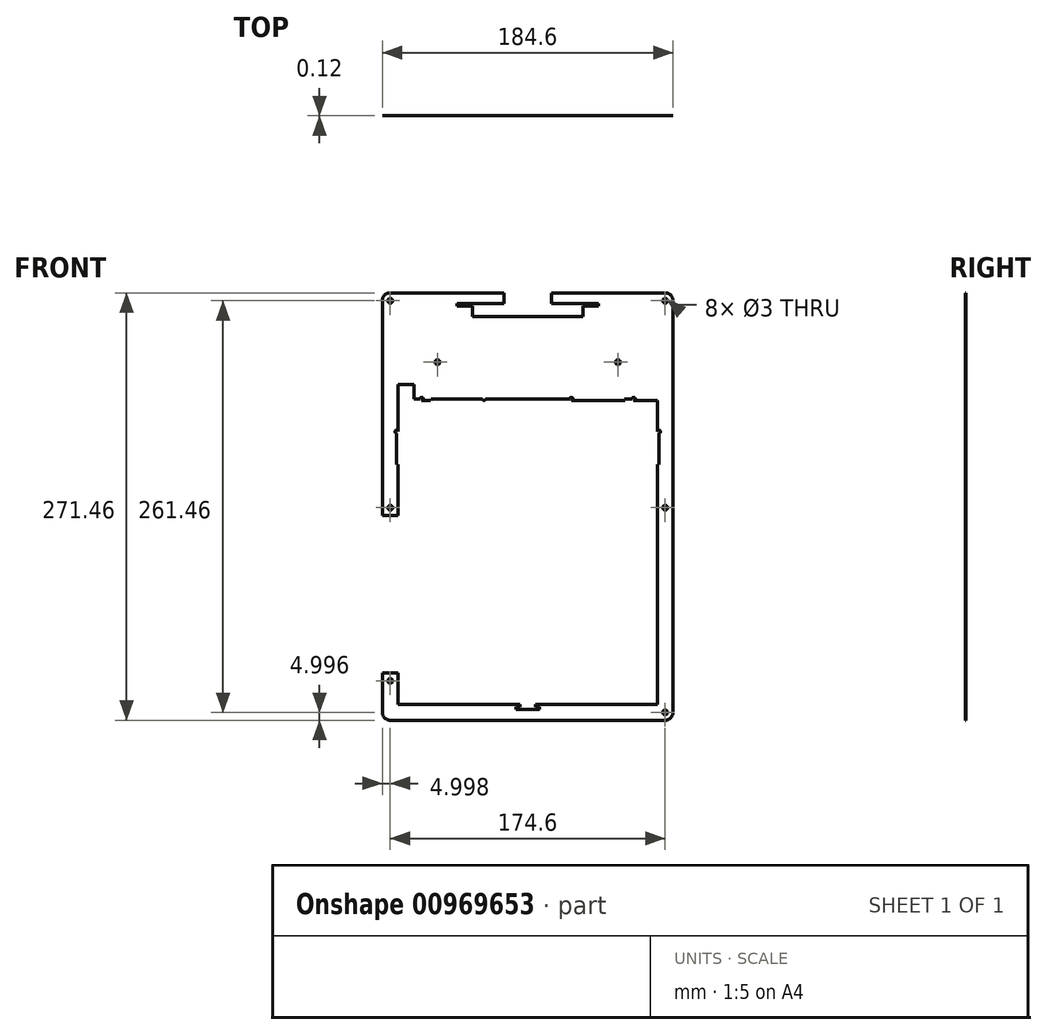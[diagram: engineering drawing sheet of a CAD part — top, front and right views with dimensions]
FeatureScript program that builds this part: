
annotation { "Feature Type Name" : "Feature", "Feature Type Description" : "" }
export const myFeature = defineFeature(function(context is Context, id is Id, definition is map)
    precondition{}
    {
        {
            var Q0;
            Q0=qCreatedBy(makeId("Front.planeOp"),FACE);
            var sketch = newSketch(context, id + "F0", { "sketchPlane" : qUnion([Q0])});
            skLineSegment(sketch, "E0.bottom", {"start": v(-64.57, 145.19) * mm, "end": v(110.03, 145.19) * mm});
            skLineSegment(sketch, "E0.top", {"start": v(-64.57, -126.27) * mm, "end": v(110.03, -126.27) * mm});
            skLineSegment(sketch, "E0.left", {"start": v(-69.57, 140.19) * mm, "end": v(-69.57, -121.27) * mm});
            skLineSegment(sketch, "E0.right", {"start": v(115.03, 140.19) * mm, "end": v(115.03, -121.27) * mm});
            skPoint(sketch, "E1.visualSharp", {"position": v(-69.57, 145.19) * mm});
            skArc(sketch, "E1.filletArc", {"start": v(-64.57, 145.19) * mm, "mid": v(-68.1, 143.72) * mm, "end": v(-69.57, 140.19) * mm});
            skPoint(sketch, "E2.visualSharp", {"position": v(115.03, 145.19) * mm});
            skArc(sketch, "E2.filletArc", {"start": v(115.03, 140.19) * mm, "mid": v(113.56, 143.72) * mm, "end": v(110.03, 145.19) * mm});
            skPoint(sketch, "E3.visualSharp", {"position": v(-69.57, -126.27) * mm});
            skArc(sketch, "E3.filletArc", {"start": v(-69.57, -121.27) * mm, "mid": v(-68.1, -124.8) * mm, "end": v(-64.57, -126.27) * mm});
            skPoint(sketch, "E4.visualSharp", {"position": v(115.03, -126.27) * mm});
            skArc(sketch, "E4.filletArc", {"start": v(110.03, -126.27) * mm, "mid": v(113.56, -124.8) * mm, "end": v(115.03, -121.27) * mm});
            skCircle(sketch, "E5", {"center": v(-64.57, 140.19) * mm, "radius": 1.5 * mm});
            skCircle(sketch, "E6", {"center": v(110.03, 140.19) * mm, "radius": 1.5 * mm});
            skCircle(sketch, "E7", {"center": v(110.03, -121.27) * mm, "radius": 1.5 * mm});
            skCircle(sketch, "E8", {"center": v(-64.57, -101.27) * mm, "radius": 1.5 * mm});
            skLineSegment(sketch, "E9.bottom", {"start": v(-59.57, 135.19) * mm, "end": v(105.03, 135.19) * mm});
            skLineSegment(sketch, "E9.top", {"start": v(-59.57, -116.27) * mm, "end": v(105.03, -116.27) * mm});
            skLineSegment(sketch, "E9.left", {"start": v(-59.57, 135.19) * mm, "end": v(-59.57, -116.27) * mm});
            skLineSegment(sketch, "E9.right", {"start": v(105.03, 135.19) * mm, "end": v(105.03, -116.27) * mm});
            skLineSegment(sketch, "E10.bottom", {"start": v(17.73, -116.27) * mm, "end": v(27.73, -116.27) * mm});
            skLineSegment(sketch, "E10.top", {"start": v(17.73, -117.75) * mm, "end": v(27.73, -117.75) * mm});
            skLineSegment(sketch, "E10.left", {"start": v(17.73, -116.27) * mm, "end": v(17.73, -117.75) * mm});
            skLineSegment(sketch, "E10.right", {"start": v(27.73, -116.27) * mm, "end": v(27.73, -117.75) * mm});
            skLineSegment(sketch, "E11.bottom", {"start": v(15.23, -117.75) * mm, "end": v(30.23, -117.75) * mm});
            skLineSegment(sketch, "E11.top", {"start": v(15.23, -119.35) * mm, "end": v(30.23, -119.35) * mm});
            skLineSegment(sketch, "E11.left", {"start": v(15.23, -117.75) * mm, "end": v(15.23, -119.35) * mm});
            skLineSegment(sketch, "E11.right", {"start": v(30.23, -117.75) * mm, "end": v(30.23, -119.35) * mm});
            skLineSegment(sketch, "E12.bottom", {"start": v(-12.27, 135.19) * mm, "end": v(57.73, 135.19) * mm});
            skLineSegment(sketch, "E12.top", {"start": v(-12.27, 136.79) * mm, "end": v(57.73, 136.79) * mm});
            skLineSegment(sketch, "E12.left", {"start": v(-12.27, 135.19) * mm, "end": v(-12.27, 136.79) * mm});
            skLineSegment(sketch, "E12.right", {"start": v(57.73, 135.19) * mm, "end": v(57.73, 136.79) * mm});
            skLineSegment(sketch, "E13.bottom", {"start": v(-22.27, 138.49) * mm, "end": v(67.73, 138.49) * mm});
            skLineSegment(sketch, "E13.top", {"start": v(-22.27, 136.79) * mm, "end": v(67.73, 136.79) * mm});
            skLineSegment(sketch, "E13.left", {"start": v(-22.27, 138.49) * mm, "end": v(-22.27, 136.79) * mm});
            skLineSegment(sketch, "E13.right", {"start": v(67.73, 138.49) * mm, "end": v(67.73, 136.79) * mm});
            skLineSegment(sketch, "E14.bottom", {"start": v(7.73, 145.19) * mm, "end": v(37.73, 145.19) * mm});
            skLineSegment(sketch, "E14.top", {"start": v(7.73, 138.49) * mm, "end": v(37.73, 138.49) * mm});
            skLineSegment(sketch, "E14.left", {"start": v(7.73, 145.19) * mm, "end": v(7.73, 138.49) * mm});
            skLineSegment(sketch, "E14.right", {"start": v(37.73, 145.19) * mm, "end": v(37.73, 138.49) * mm});
            skLineSegment(sketch, "E15.bottom", {"start": v(-59.57, 36.13) * mm, "end": v(105.03, 36.13) * mm});
            skLineSegment(sketch, "E15.top", {"start": v(-59.57, 35.13) * mm, "end": v(105.03, 35.13) * mm});
            skLineSegment(sketch, "E15.left", {"start": v(-59.57, 36.13) * mm, "end": v(-59.57, 35.13) * mm});
            skLineSegment(sketch, "E15.right", {"start": v(105.03, 36.13) * mm, "end": v(105.03, 35.13) * mm});
            skLineSegment(sketch, "E16.bottom", {"start": v(-62.57, 35.13) * mm, "end": v(108.03, 35.13) * mm});
            skLineSegment(sketch, "E16.top", {"start": v(-62.57, 33.13) * mm, "end": v(108.03, 33.13) * mm});
            skLineSegment(sketch, "E16.left", {"start": v(-62.57, 35.13) * mm, "end": v(-62.57, 33.13) * mm});
            skLineSegment(sketch, "E16.right", {"start": v(108.03, 35.13) * mm, "end": v(108.03, 33.13) * mm});
            skLineSegment(sketch, "E17.bottom", {"start": v(108.03, 33.13) * mm, "end": v(105.03, 33.13) * mm});
            skLineSegment(sketch, "E17.top", {"start": v(108.03, 34.53) * mm, "end": v(105.03, 34.53) * mm});
            skLineSegment(sketch, "E17.left", {"start": v(108.03, 33.13) * mm, "end": v(108.03, 34.53) * mm});
            skLineSegment(sketch, "E17.right", {"start": v(105.03, 33.13) * mm, "end": v(105.03, 34.53) * mm});
            skLineSegment(sketch, "E18.bottom", {"start": v(-62.57, 33.13) * mm, "end": v(-59.57, 33.13) * mm});
            skLineSegment(sketch, "E18.top", {"start": v(-62.57, 34.53) * mm, "end": v(-59.57, 34.53) * mm});
            skLineSegment(sketch, "E18.left", {"start": v(-62.57, 33.13) * mm, "end": v(-62.57, 34.53) * mm});
            skLineSegment(sketch, "E18.right", {"start": v(-59.57, 33.13) * mm, "end": v(-59.57, 34.53) * mm});
            skLineSegment(sketch, "E19.top", {"start": v(-59.57, 66.13) * mm, "end": v(105.03, 66.13) * mm});
            skLineSegment(sketch, "E19.left", {"start": v(-59.57, 36.13) * mm, "end": v(-59.57, 66.13) * mm});
            skLineSegment(sketch, "E19.right", {"start": v(105.03, 36.13) * mm, "end": v(105.03, 66.13) * mm});
            skLineSegment(sketch, "E20.top", {"start": v(-59.57, 76.88) * mm, "end": v(105.03, 76.88) * mm});
            skLineSegment(sketch, "E20.left", {"start": v(-59.57, 36.13) * mm, "end": v(-59.57, 76.88) * mm});
            skLineSegment(sketch, "E20.right", {"start": v(105.03, 36.13) * mm, "end": v(105.03, 76.88) * mm});
            skLineSegment(sketch, "E21.bottom", {"start": v(-52.27, 66.13) * mm, "end": v(97.73, 66.13) * mm});
            skLineSegment(sketch, "E21.top", {"start": v(-52.27, 36.13) * mm, "end": v(97.73, 36.13) * mm});
            skLineSegment(sketch, "E21.left", {"start": v(-52.27, 66.13) * mm, "end": v(-52.27, 36.13) * mm});
            skLineSegment(sketch, "E21.right", {"start": v(97.73, 66.13) * mm, "end": v(97.73, 36.13) * mm});
            skLineSegment(sketch, "E22.bottom", {"start": v(-55.27, 36.13) * mm, "end": v(100.73, 36.13) * mm});
            skLineSegment(sketch, "E22.top", {"start": v(-55.27, 69.13) * mm, "end": v(100.73, 69.13) * mm});
            skLineSegment(sketch, "E22.left", {"start": v(-55.27, 36.13) * mm, "end": v(-55.27, 69.13) * mm});
            skLineSegment(sketch, "E22.right", {"start": v(100.73, 36.13) * mm, "end": v(100.73, 69.13) * mm});
            skLineSegment(sketch, "E23.bottom", {"start": v(-58.27, 72.13) * mm, "end": v(103.73, 72.13) * mm});
            skLineSegment(sketch, "E23.top", {"start": v(-58.27, 33.13) * mm, "end": v(103.73, 33.13) * mm});
            skLineSegment(sketch, "E23.left", {"start": v(-58.27, 72.13) * mm, "end": v(-58.27, 33.13) * mm});
            skLineSegment(sketch, "E23.right", {"start": v(103.73, 72.13) * mm, "end": v(103.73, 33.13) * mm});
            skLineSegment(sketch, "E24.top", {"start": v(-12.27, 130.19) * mm, "end": v(57.73, 130.19) * mm});
            skLineSegment(sketch, "E24.left", {"start": v(-12.27, 135.19) * mm, "end": v(-12.27, 130.19) * mm});
            skLineSegment(sketch, "E24.right", {"start": v(57.73, 135.19) * mm, "end": v(57.73, 130.19) * mm});
            skLineSegment(sketch, "E25.bottom", {"start": v(-59.57, 33.13) * mm, "end": v(105.03, 33.13) * mm});
            skLineSegment(sketch, "E25.top", {"start": v(-59.57, 23.13) * mm, "end": v(105.03, 23.13) * mm});
            skLineSegment(sketch, "E25.left", {"start": v(-59.57, 33.13) * mm, "end": v(-59.57, 23.13) * mm});
            skLineSegment(sketch, "E25.right", {"start": v(105.03, 33.13) * mm, "end": v(105.03, 23.13) * mm});
            skLineSegment(sketch, "E26.bottom", {"start": v(-69.57, -96.27) * mm, "end": v(-59.57, -96.27) * mm});
            skLineSegment(sketch, "E26.top", {"start": v(-69.57, 3.73) * mm, "end": v(-59.57, 3.73) * mm});
            skLineSegment(sketch, "E26.left", {"start": v(-69.57, -96.27) * mm, "end": v(-69.57, 3.73) * mm});
            skLineSegment(sketch, "E26.right", {"start": v(-59.57, -96.27) * mm, "end": v(-59.57, 3.73) * mm});
            skLineSegment(sketch, "E27", {"start": v(-12.27, 130.19) * mm, "end": v(-59.57, 36.13) * mm});
            skLineSegment(sketch, "E28", {"start": v(57.73, 130.19) * mm, "end": v(105.03, 36.13) * mm});
            skCircle(sketch, "E29", {"center": v(-34.57, 101.13) * mm, "radius": 1.5 * mm});
            skCircle(sketch, "E30", {"center": v(80.03, 101.13) * mm, "radius": 1.5 * mm});
            skLineSegment(sketch, "E31.top", {"start": v(7.73, 23.13) * mm, "end": v(37.73, 23.13) * mm});
            skLineSegment(sketch, "E31.left", {"start": v(7.73, 138.49) * mm, "end": v(7.73, 23.13) * mm});
            skLineSegment(sketch, "E31.right", {"start": v(37.73, 138.49) * mm, "end": v(37.73, 23.13) * mm});
            skLineSegment(sketch, "E32.bottom", {"start": v(-59.57, 76.88) * mm, "end": v(7.73, 76.88) * mm});
            skLineSegment(sketch, "E33.bottom", {"start": v(-59.57, 36.13) * mm, "end": v(-39.57, 36.13) * mm});
            skLineSegment(sketch, "E33.top", {"start": v(-59.57, 76.88) * mm, "end": v(-39.57, 76.88) * mm});
            skLineSegment(sketch, "E33.right", {"start": v(-39.57, 36.13) * mm, "end": v(-39.57, 76.88) * mm});
            skLineSegment(sketch, "E34.bottom", {"start": v(105.03, 76.88) * mm, "end": v(85.03, 76.88) * mm});
            skLineSegment(sketch, "E34.top", {"start": v(105.03, 36.13) * mm, "end": v(85.03, 36.13) * mm});
            skLineSegment(sketch, "E34.left", {"start": v(105.03, 76.88) * mm, "end": v(105.03, 36.13) * mm});
            skLineSegment(sketch, "E34.right", {"start": v(85.03, 76.88) * mm, "end": v(85.03, 36.13) * mm});
            skLineSegment(sketch, "E35.bottom", {"start": v(105.03, 23.13) * mm, "end": v(95.03, 23.13) * mm});
            skLineSegment(sketch, "E35.top", {"start": v(105.03, 36.13) * mm, "end": v(95.03, 36.13) * mm});
            skLineSegment(sketch, "E35.left", {"start": v(105.03, 23.13) * mm, "end": v(105.03, 36.13) * mm});
            skLineSegment(sketch, "E35.right", {"start": v(95.03, 23.13) * mm, "end": v(95.03, 36.13) * mm});
            skLineSegment(sketch, "E36.bottom", {"start": v(-49.57, 23.13) * mm, "end": v(-59.57, 23.13) * mm});
            skLineSegment(sketch, "E36.top", {"start": v(-49.57, 36.13) * mm, "end": v(-59.57, 36.13) * mm});
            skLineSegment(sketch, "E36.left", {"start": v(-49.57, 23.13) * mm, "end": v(-49.57, 36.13) * mm});
            skLineSegment(sketch, "E36.right", {"start": v(-59.57, 23.13) * mm, "end": v(-59.57, 36.13) * mm});
            skLineSegment(sketch, "E37.top", {"start": v(-49.57, 86.93) * mm, "end": v(-59.57, 86.93) * mm});
            skLineSegment(sketch, "E37.left", {"start": v(-49.57, 36.13) * mm, "end": v(-49.57, 86.93) * mm});
            skLineSegment(sketch, "E37.right", {"start": v(-59.57, 36.13) * mm, "end": v(-59.57, 86.93) * mm});
            skCircle(sketch, "E38", {"center": v(-64.57, 8.73) * mm, "radius": 1.5 * mm});
            skCircle(sketch, "E39", {"center": v(110.03, 8.73) * mm, "radius": 1.5 * mm});
            skLineSegment(sketch, "E40.bottom", {"start": v(-60.57, 36.13) * mm, "end": v(106.03, 36.13) * mm});
            skLineSegment(sketch, "E40.top", {"start": v(-60.57, 77.88) * mm, "end": v(106.03, 77.88) * mm});
            skLineSegment(sketch, "E40.left", {"start": v(-60.57, 36.13) * mm, "end": v(-60.57, 77.88) * mm});
            skLineSegment(sketch, "E40.right", {"start": v(106.03, 36.13) * mm, "end": v(106.03, 77.88) * mm});
            skCircle(sketch, "E41", {"center": v(-60.57, 57) * mm, "radius": 1 * mm});
            skCircle(sketch, "E42", {"center": v(106.03, 57.05) * mm, "radius": 1 * mm});
            skCircle(sketch, "E43", {"center": v(-5.04, 77.88) * mm, "radius": 1 * mm});
            skCircle(sketch, "E44", {"center": v(50.5, 77.88) * mm, "radius": 1 * mm});
            skLineSegment(sketch, "E45.bottom", {"start": v(-54.57, 18.13) * mm, "end": v(100.03, 18.13) * mm});
            skLineSegment(sketch, "E45.top", {"start": v(-54.57, -111.27) * mm, "end": v(100.03, -111.27) * mm});
            skLineSegment(sketch, "E45.left", {"start": v(-54.57, 18.13) * mm, "end": v(-54.57, -111.27) * mm});
            skLineSegment(sketch, "E45.right", {"start": v(100.03, 18.13) * mm, "end": v(100.03, -111.27) * mm});
            skCircle(sketch, "E46", {"center": v(-54.57, 18.13) * mm, "radius": 1 * mm});
            skCircle(sketch, "E47", {"center": v(100.03, 18.13) * mm, "radius": 1 * mm});
            skCircle(sketch, "E48", {"center": v(100.03, -111.27) * mm, "radius": 1 * mm});
            skCircle(sketch, "E49", {"center": v(-54.57, -111.27) * mm, "radius": 1 * mm});
            skCircle(sketch, "E50", {"center": v(-44.57, 77.88) * mm, "radius": 1 * mm});
            skCircle(sketch, "E51", {"center": v(90.03, 77.88) * mm, "radius": 1 * mm});
            skSolve(sketch);
        }
        {
            var Q0;
            Q0=makeQuery(id+"F0.imprint","IMPRINT",FACE,{"disambiguationData":[TD([[makeQuery(id+"F0.imprint","IMPRINT",EDGE,{"derivedFrom":sQuery(id+"F0.wireOp",EDGE,"E0.top")}),1.0]])]});
            var Q1;
            {var subQ0=sQuery(id+"F0.wireOp",EDGE,"E16.left");Q1=makeQuery(id+"F0.imprint","IMPRINT",FACE,{"disambiguationData":[TD([[makeQuery(id+"F0.imprint","IMPRINT",EDGE,{"derivedFrom":subQ0}),1.0]])]});}
            var Q2;
            {var subQ0=sQuery(id+"F0.wireOp",EDGE,"E16.right");Q2=makeQuery(id+"F0.imprint","IMPRINT",FACE,{"disambiguationData":[TD([[makeQuery(id+"F0.imprint","IMPRINT",EDGE,{"derivedFrom":subQ0}),-1.0]])]});}
            var Q3;
            {var subQ0=sQuery(id+"F0.wireOp",EDGE,"E31.left");var subQ1=sQuery(id+"F0.wireOp",EDGE,"E24.top");var subQ2=makeQuery(id+"F0.imprint","INTERSECT",VERTEX,{"derivedFrom":[subQ1,subQ0]});Q3=makeQuery(id+"F0.imprint","IMPRINT",FACE,{"disambiguationData":[TD([[makeQuery(id+"F0.imprint","IMPRINT",EDGE,{"disambiguationData":[TD([[subQ2,-1.0]])],"derivedFrom":subQ0}),-1.0]])]});}
            var Q4;
            {var subQ0=sQuery(id+"F0.wireOp",EDGE,"E31.right");var subQ1=sQuery(id+"F0.wireOp",EDGE,"E25.bottom");var subQ2=makeQuery(id+"F0.imprint","INTERSECT",VERTEX,{"derivedFrom":[subQ1,subQ0]});Q4=makeQuery(id+"F0.imprint","IMPRINT",FACE,{"disambiguationData":[TD([[makeQuery(id+"F0.imprint","IMPRINT",EDGE,{"disambiguationData":[TD([[subQ2,-1.0]])],"derivedFrom":subQ1}),-1.0]])]});}
            var Q5;
            {var subQ0=sQuery(id+"F0.wireOp",EDGE,"E36.left");var subQ1=sQuery(id+"F0.wireOp",EDGE,"E25.bottom");var subQ2=makeQuery(id+"F0.imprint","INTERSECT",VERTEX,{"derivedFrom":[subQ1,subQ0]});Q5=makeQuery(id+"F0.imprint","IMPRINT",FACE,{"disambiguationData":[TD([[makeQuery(id+"F0.imprint","IMPRINT",EDGE,{"disambiguationData":[TD([[subQ2,-1.0]])],"derivedFrom":subQ1}),-1.0]])]});}
            var Q6;
            {var subQ7=sQuery(id+"F0.wireOp",EDGE,"E24.right");Q6=makeQuery(id+"F0.imprint","IMPRINT",FACE,{"disambiguationData":[TD([[makeQuery(id+"F0.imprint","IMPRINT",EDGE,{"derivedFrom":subQ7}),1.0]])]});}
            var Q7;
            {var subQ0=sQuery(id+"F0.wireOp",EDGE,"E31.right");var subQ1=sQuery(id+"F0.wireOp",EDGE,"E24.top");var subQ2=makeQuery(id+"F0.imprint","INTERSECT",VERTEX,{"derivedFrom":[subQ1,subQ0]});Q7=makeQuery(id+"F0.imprint","IMPRINT",FACE,{"disambiguationData":[TD([[makeQuery(id+"F0.imprint","IMPRINT",EDGE,{"disambiguationData":[TD([[subQ2,-1.0]])],"derivedFrom":subQ0}),1.0]])]});}
            var Q8;
            {var subQ0=sQuery(id+"F0.wireOp",EDGE,"E42");var subQ1=sQuery(id+"F0.wireOp",EDGE,"E40.right");var subQ2=makeQuery(id+"F0.imprint","INTERSECT",VERTEX,{"disambiguationData":[OD(0.0)],"derivedFrom":[subQ1,subQ0]});Q8=makeQuery(id+"F0.imprint","IMPRINT",FACE,{"disambiguationData":[TD([[makeQuery(id+"F0.imprint","IMPRINT",EDGE,{"disambiguationData":[TD([[subQ2,-1.0]])],"derivedFrom":subQ1}),-1.0]])]});}
            var Q9;
            {var subQ0=sQuery(id+"F0.wireOp",EDGE,"E44");var subQ1=sQuery(id+"F0.wireOp",EDGE,"E40.top");var subQ2=makeQuery(id+"F0.imprint","INTERSECT",VERTEX,{"disambiguationData":[OD(0.0)],"derivedFrom":[subQ1,subQ0]});Q9=makeQuery(id+"F0.imprint","IMPRINT",FACE,{"disambiguationData":[TD([[makeQuery(id+"F0.imprint","IMPRINT",EDGE,{"disambiguationData":[TD([[subQ2,-1.0]])],"derivedFrom":subQ1}),1.0]])]});}
            var Q10;
            {var subQ0=sQuery(id+"F0.wireOp",EDGE,"E41");var subQ1=sQuery(id+"F0.wireOp",EDGE,"E40.left");var subQ2=makeQuery(id+"F0.imprint","INTERSECT",VERTEX,{"disambiguationData":[OD(0.0)],"derivedFrom":[subQ1,subQ0]});Q10=makeQuery(id+"F0.imprint","IMPRINT",FACE,{"disambiguationData":[TD([[makeQuery(id+"F0.imprint","IMPRINT",EDGE,{"disambiguationData":[TD([[subQ2,-1.0]])],"derivedFrom":subQ1}),1.0]])]});}
            var Q11;
            {var subQ2=sQuery(id+"F0.wireOp",EDGE,"E31.right");var subQ6=sQuery(id+"F0.wireOp",EDGE,"E16.bottom");var subQ8=makeQuery(id+"F0.imprint","INTERSECT",VERTEX,{"derivedFrom":[subQ6,subQ2]});Q11=makeQuery(id+"F0.imprint","IMPRINT",FACE,{"disambiguationData":[TD([[makeQuery(id+"F0.imprint","IMPRINT",EDGE,{"disambiguationData":[TD([[subQ8,-1.0]])],"derivedFrom":subQ6}),1.0]])]});}
            var Q12;
            {var subQ0=sQuery(id+"F0.wireOp",EDGE,"E43");var subQ1=sQuery(id+"F0.wireOp",EDGE,"E40.top");var subQ2=makeQuery(id+"F0.imprint","INTERSECT",VERTEX,{"disambiguationData":[OD(0.0)],"derivedFrom":[subQ1,subQ0]});Q12=makeQuery(id+"F0.imprint","IMPRINT",FACE,{"disambiguationData":[TD([[makeQuery(id+"F0.imprint","IMPRINT",EDGE,{"disambiguationData":[TD([[subQ2,-1.0]])],"derivedFrom":subQ1}),1.0]])]});}
            var Q13;
            {var subQ2=sQuery(id+"F0.wireOp",EDGE,"E36.left");var subQ4=sQuery(id+"F0.wireOp",EDGE,"E16.bottom");var subQ5=makeQuery(id+"F0.imprint","INTERSECT",VERTEX,{"derivedFrom":[subQ4,subQ2]});Q13=makeQuery(id+"F0.imprint","IMPRINT",FACE,{"disambiguationData":[TD([[makeQuery(id+"F0.imprint","IMPRINT",EDGE,{"disambiguationData":[TD([[subQ5,-1.0]])],"derivedFrom":subQ4}),1.0]])]});}
            var Q14;
            {var subQ0=sQuery(id+"F0.wireOp",EDGE,"E44");var subQ1=sQuery(id+"F0.wireOp",EDGE,"E40.top");var subQ2=makeQuery(id+"F0.imprint","INTERSECT",VERTEX,{"disambiguationData":[OD(0.0)],"derivedFrom":[subQ1,subQ0]});Q14=makeQuery(id+"F0.imprint","IMPRINT",FACE,{"disambiguationData":[TD([[makeQuery(id+"F0.imprint","IMPRINT",EDGE,{"disambiguationData":[TD([[subQ2,-1.0]])],"derivedFrom":subQ1}),-1.0]])]});}
            var Q15;
            {var subQ0=sQuery(id+"F0.wireOp",EDGE,"E42");var subQ1=sQuery(id+"F0.wireOp",EDGE,"E40.right");var subQ2=makeQuery(id+"F0.imprint","INTERSECT",VERTEX,{"disambiguationData":[OD(0.0)],"derivedFrom":[subQ1,subQ0]});Q15=makeQuery(id+"F0.imprint","IMPRINT",FACE,{"disambiguationData":[TD([[makeQuery(id+"F0.imprint","IMPRINT",EDGE,{"disambiguationData":[TD([[subQ2,-1.0]])],"derivedFrom":subQ1}),1.0]])]});}
            var Q16;
            {var subQ0=sQuery(id+"F0.wireOp",EDGE,"E43");var subQ1=sQuery(id+"F0.wireOp",EDGE,"E40.top");var subQ2=makeQuery(id+"F0.imprint","INTERSECT",VERTEX,{"disambiguationData":[OD(0.0)],"derivedFrom":[subQ1,subQ0]});Q16=makeQuery(id+"F0.imprint","IMPRINT",FACE,{"disambiguationData":[TD([[makeQuery(id+"F0.imprint","IMPRINT",EDGE,{"disambiguationData":[TD([[subQ2,-1.0]])],"derivedFrom":subQ1}),-1.0]])]});}
            var Q17;
            {var subQ0=sQuery(id+"F0.wireOp",EDGE,"E41");var subQ1=sQuery(id+"F0.wireOp",EDGE,"E40.left");var subQ2=makeQuery(id+"F0.imprint","INTERSECT",VERTEX,{"disambiguationData":[OD(0.0)],"derivedFrom":[subQ1,subQ0]});Q17=makeQuery(id+"F0.imprint","IMPRINT",FACE,{"disambiguationData":[TD([[makeQuery(id+"F0.imprint","IMPRINT",EDGE,{"disambiguationData":[TD([[subQ2,-1.0]])],"derivedFrom":subQ1}),-1.0]])]});}
            var Q18;
            {var subQ6=sQuery(id+"F0.wireOp",EDGE,"E1.filletArc");Q18=makeQuery(id+"F0.imprint","IMPRINT",FACE,{"disambiguationData":[TD([[makeQuery(id+"F0.imprint","IMPRINT",EDGE,{"derivedFrom":subQ6}),1.0]])]});}
            var Q19;
            {var subQ5=sQuery(id+"F0.wireOp",EDGE,"E24.left");Q19=makeQuery(id+"F0.imprint","IMPRINT",FACE,{"disambiguationData":[TD([[makeQuery(id+"F0.imprint","IMPRINT",EDGE,{"derivedFrom":subQ5}),-1.0]])]});}
            var Q20;
            {var subQ0=sQuery(id+"F0.wireOp",EDGE,"E51");var subQ1=sQuery(id+"F0.wireOp",EDGE,"E40.top");var subQ2=makeQuery(id+"F0.imprint","INTERSECT",VERTEX,{"disambiguationData":[OD(0.0)],"derivedFrom":[subQ1,subQ0]});Q20=makeQuery(id+"F0.imprint","IMPRINT",FACE,{"disambiguationData":[TD([[makeQuery(id+"F0.imprint","IMPRINT",EDGE,{"disambiguationData":[TD([[subQ2,-1.0]])],"derivedFrom":subQ1}),-1.0]])]});}
            var Q21;
            {var subQ0=sQuery(id+"F0.wireOp",EDGE,"E51");var subQ1=sQuery(id+"F0.wireOp",EDGE,"E40.top");var subQ2=makeQuery(id+"F0.imprint","INTERSECT",VERTEX,{"disambiguationData":[OD(0.0)],"derivedFrom":[subQ1,subQ0]});Q21=makeQuery(id+"F0.imprint","IMPRINT",FACE,{"disambiguationData":[TD([[makeQuery(id+"F0.imprint","IMPRINT",EDGE,{"disambiguationData":[TD([[subQ2,-1.0]])],"derivedFrom":subQ1}),1.0]])]});}
            var Q22;
            {var subQ0=sQuery(id+"F0.wireOp",EDGE,"E50");var subQ1=sQuery(id+"F0.wireOp",EDGE,"E40.top");var subQ2=makeQuery(id+"F0.imprint","INTERSECT",VERTEX,{"disambiguationData":[OD(0.0)],"derivedFrom":[subQ1,subQ0]});Q22=makeQuery(id+"F0.imprint","IMPRINT",FACE,{"disambiguationData":[TD([[makeQuery(id+"F0.imprint","IMPRINT",EDGE,{"disambiguationData":[TD([[subQ2,-1.0]])],"derivedFrom":subQ1}),-1.0]])]});}
            var Q23;
            {var subQ0=sQuery(id+"F0.wireOp",EDGE,"E50");var subQ1=sQuery(id+"F0.wireOp",EDGE,"E40.top");var subQ2=makeQuery(id+"F0.imprint","INTERSECT",VERTEX,{"disambiguationData":[OD(0.0)],"derivedFrom":[subQ1,subQ0]});Q23=makeQuery(id+"F0.imprint","IMPRINT",FACE,{"disambiguationData":[TD([[makeQuery(id+"F0.imprint","IMPRINT",EDGE,{"disambiguationData":[TD([[subQ2,-1.0]])],"derivedFrom":subQ1}),1.0]])]});}
            var Q24;
            {var subQ1=sQuery(id+"F0.wireOp",EDGE,"E36.bottom");Q24=makeQuery(id+"F0.imprint","IMPRINT",FACE,{"disambiguationData":[TD([[makeQuery(id+"F0.imprint","IMPRINT",EDGE,{"derivedFrom":subQ1}),-1.0]])]});}
            var Q25;
            {var subQ2=sQuery(id+"F0.wireOp",EDGE,"E23.left");var subQ6=sQuery(id+"F0.wireOp",EDGE,"E16.bottom");var subQ8=makeQuery(id+"F0.imprint","INTERSECT",VERTEX,{"derivedFrom":[subQ6,subQ2]});Q25=makeQuery(id+"F0.imprint","IMPRINT",FACE,{"disambiguationData":[TD([[makeQuery(id+"F0.imprint","IMPRINT",EDGE,{"disambiguationData":[TD([[subQ8,-1.0]])],"derivedFrom":subQ6}),1.0]])]});}
            var Q26;
            {var subQ0=sQuery(id+"F0.wireOp",EDGE,"E36.right");var subQ1=sQuery(id+"F0.wireOp",EDGE,"E16.bottom");var subQ2=makeQuery(id+"F0.imprint","INTERSECT",VERTEX,{"derivedFrom":[subQ1,subQ0]});Q26=makeQuery(id+"F0.imprint","IMPRINT",FACE,{"disambiguationData":[TD([[makeQuery(id+"F0.imprint","IMPRINT",EDGE,{"disambiguationData":[TD([[subQ2,-1.0]])],"derivedFrom":subQ1}),1.0]])]});}
            var Q27;
            {var subQ0=sQuery(id+"F0.wireOp",EDGE,"E31.left");var subQ1=sQuery(id+"F0.wireOp",EDGE,"E16.bottom");var subQ2=makeQuery(id+"F0.imprint","INTERSECT",VERTEX,{"derivedFrom":[subQ1,subQ0]});Q27=makeQuery(id+"F0.imprint","IMPRINT",FACE,{"disambiguationData":[TD([[makeQuery(id+"F0.imprint","IMPRINT",EDGE,{"disambiguationData":[TD([[subQ2,-1.0]])],"derivedFrom":subQ1}),1.0]])]});}
            var Q28;
            {var subQ5=sQuery(id+"F0.wireOp",EDGE,"E31.top");Q28=makeQuery(id+"F0.imprint","IMPRINT",FACE,{"disambiguationData":[TD([[makeQuery(id+"F0.imprint","IMPRINT",EDGE,{"derivedFrom":subQ5}),1.0]])]});}
            var Q29;
            {var subQ2=sQuery(id+"F0.wireOp",EDGE,"E35.right");var subQ4=sQuery(id+"F0.wireOp",EDGE,"E16.bottom");var subQ5=makeQuery(id+"F0.imprint","INTERSECT",VERTEX,{"derivedFrom":[subQ4,subQ2]});Q29=makeQuery(id+"F0.imprint","IMPRINT",FACE,{"disambiguationData":[TD([[makeQuery(id+"F0.imprint","IMPRINT",EDGE,{"disambiguationData":[TD([[subQ5,-1.0]])],"derivedFrom":subQ4}),1.0]])]});}
            var Q30;
            {var subQ0=sQuery(id+"F0.wireOp",EDGE,"E23.right");var subQ1=sQuery(id+"F0.wireOp",EDGE,"E16.bottom");var subQ2=makeQuery(id+"F0.imprint","INTERSECT",VERTEX,{"derivedFrom":[subQ1,subQ0]});Q30=makeQuery(id+"F0.imprint","IMPRINT",FACE,{"disambiguationData":[TD([[makeQuery(id+"F0.imprint","IMPRINT",EDGE,{"disambiguationData":[TD([[subQ2,-1.0]])],"derivedFrom":subQ1}),1.0]])]});}
            var Q31;
            {var subQ3=sQuery(id+"F0.wireOp",EDGE,"E35.bottom");Q31=makeQuery(id+"F0.imprint","IMPRINT",FACE,{"disambiguationData":[TD([[makeQuery(id+"F0.imprint","IMPRINT",EDGE,{"derivedFrom":subQ3}),-1.0]])]});}
            var Q32;
            {var subQ0=sQuery(id+"F0.wireOp",EDGE,"E31.left");var subQ1=sQuery(id+"F0.wireOp",EDGE,"E24.top");var subQ2=makeQuery(id+"F0.imprint","INTERSECT",VERTEX,{"derivedFrom":[subQ1,subQ0]});Q32=makeQuery(id+"F0.imprint","IMPRINT",FACE,{"disambiguationData":[TD([[makeQuery(id+"F0.imprint","IMPRINT",EDGE,{"disambiguationData":[TD([[subQ2,-1.0]])],"derivedFrom":subQ1}),-1.0]])]});}
            extrude(context, id + "F1", {"entities" : qUnion([Q0, Q1, Q2, Q3, Q4, Q5, Q6, Q7, Q8, Q9, Q10, Q11, Q12, Q13, Q14, Q15, Q16, Q17, Q18, Q19, Q20, Q21, Q22, Q23, Q24, Q25, Q26, Q27, Q28, Q29, Q30, Q31, Q32]), "depth" : .118 * mm, "offsetDistance" : 25 * mm});
        }
    });
